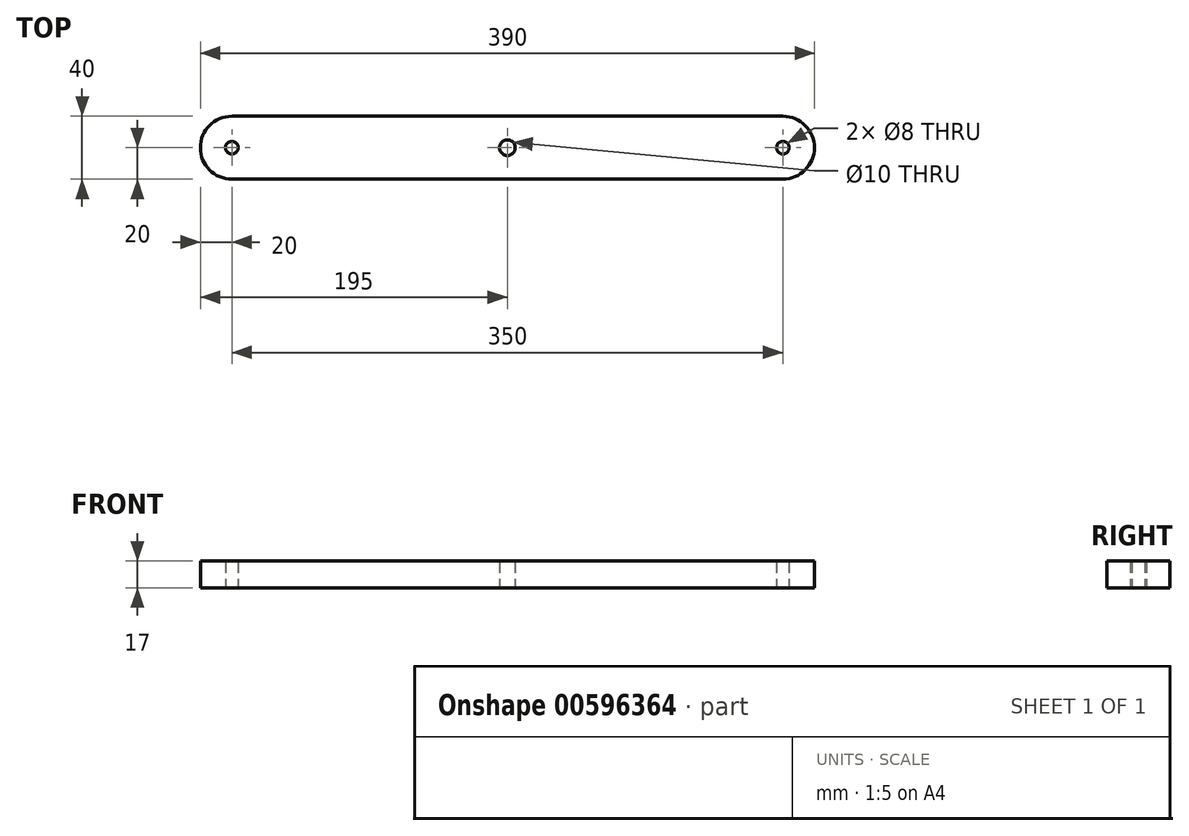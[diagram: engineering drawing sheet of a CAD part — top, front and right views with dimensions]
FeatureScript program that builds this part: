
annotation { "Feature Type Name" : "Feature", "Feature Type Description" : "" }
export const myFeature = defineFeature(function(context is Context, id is Id, definition is map)
    precondition{}
    {
        {
            var Q0;
            Q0=qCreatedBy(makeId("Top.planeOp"),FACE);
            var sketch = newSketch(context, id + "F0", { "sketchPlane" : qUnion([Q0])});
            skLineSegment(sketch, "E0.bottom", {"start": v(175, 20) * mm, "end": v(-175, 20) * mm});
            skLineSegment(sketch, "E0.top", {"start": v(175, -20) * mm, "end": v(-175, -20) * mm});
            skPoint(sketch, "E0.middle", {"position": v(0, 0) * mm});
            skCircle(sketch, "E1", {"center": v(-175, 0) * mm, "radius": 4 * mm});
            skCircle(sketch, "E2", {"center": v(175, 0) * mm, "radius": 4 * mm});
            skCircle(sketch, "E3", {"center": v(0, 0) * mm, "radius": 5 * mm});
            skArc(sketch, "E4", {"start": v(-175, 20) * mm, "mid": v(-195, 0) * mm, "end": v(-175, -20) * mm});
            skLineSegment(sketch, "E5", {"start": v(-175, 47.26) * mm, "end": v(-175, -53.35) * mm, "construction": true});
            skLineSegment(sketch, "E6", {"start": v(175, 56.25) * mm, "end": v(175, -52.75) * mm, "construction": true});
            skArc(sketch, "E7", {"start": v(175, -20) * mm, "mid": v(195, 0) * mm, "end": v(175, 20) * mm});
            skSolve(sketch);
        }
        {
            var Q0;
            Q0=makeQuery(id+"F0.imprint","IMPRINT",FACE,{"disambiguationData":[TD([[makeQuery(id+"F0.imprint","IMPRINT",EDGE,{"derivedFrom":sQuery(id+"F0.wireOp",EDGE,"E0.bottom")}),1.0]])]});
            extrude(context, id + "F1", {"entities" : qUnion([Q0]), "endBound" : BoundingType.SYMMETRIC, "depth" : 17 * mm, "offsetDistance" : 25 * mm});
        }
    });
